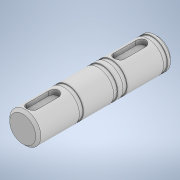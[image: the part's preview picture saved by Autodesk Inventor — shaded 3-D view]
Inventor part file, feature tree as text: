
AUTODESK INVENTOR PART (.ipt)
format: ipt  version: 2021 (Build 250183000, 183)  size: 279,040 bytes
history: native  units: mm
features: revolve x2, plane x1, extrude x1, chamfer x1, sketch x1, projected_geometry x1
ambient origin geometry x8: Origin, YZ Plane, XZ Plane, XY Plane, X Axis, Y Axis, Z Axis, Center Point
bodies: Solid1 (feature_tree)
feature tree (7):
  revolve  "Revolution1"  [1 undecoded]
  revolve  "Revolution2"  Angle=90.0deg
  plane  "Work Plane2"
  extrude  "Extrusion2"  TaperAngle=90.0deg  [1 undecoded]
  chamfer  "Chamfer3"  Distance=2.85mm
  sketch  "Sketch1"  dims[d0=3.0mm d1=25.9mm d2=90.0deg d4=90.0deg d33=2.85mm d34=0.8mm d35=2.85mm d49=6.15mm d50=1.0mm d52=1.0mm d53=0.0mm d54=0.5mm d55=2.0mm d56=45.0deg d57=5.8mm d58=7.0mm d59=1.0mm d60=3.5mm d61=3.5mm d63=1.0mm d64=6.15mm d65=1.0mm d66=1.75mm]
  projected_geometry  "Projected Loop4"
note: 2 required parameter values undecoded (feature->parameter linkage not recoverable at this tier; creation-order binding heuristic only, values carry confidence <= 0.55)